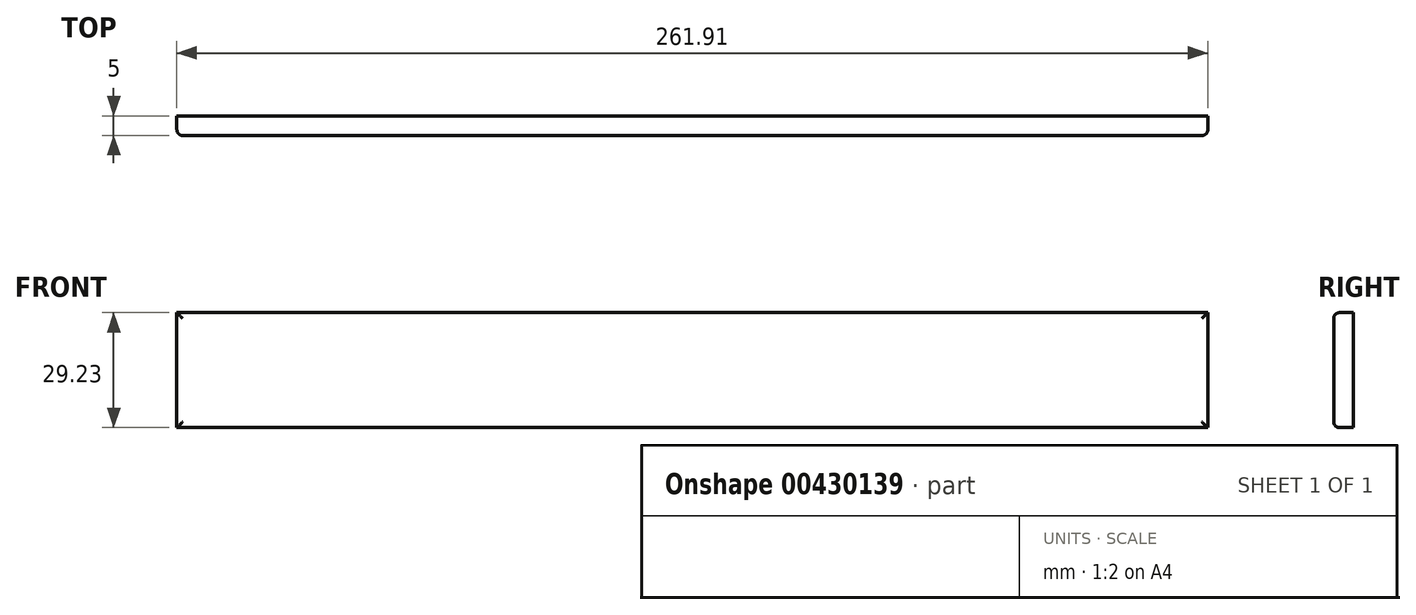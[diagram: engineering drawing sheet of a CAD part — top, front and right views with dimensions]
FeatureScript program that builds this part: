
annotation { "Feature Type Name" : "Feature", "Feature Type Description" : "" }
export const myFeature = defineFeature(function(context is Context, id is Id, definition is map)
    precondition{}
    {
        {
            var Q0;
            Q0=qCreatedBy(makeId("Front.planeOp"),FACE);
            var sketch = newSketch(context, id + "F0", { "sketchPlane" : qUnion([Q0])});
            skLineSegment(sketch, "E0.bottom", {"start": v(-90.82, 32.53) * mm, "end": v(90.82, 32.53) * mm});
            skLineSegment(sketch, "E0.top", {"start": v(-90.82, -25.4) * mm, "end": v(90.82, -25.4) * mm});
            skLineSegment(sketch, "E0.left", {"start": v(-90.82, 32.53) * mm, "end": v(-90.82, -25.4) * mm});
            skLineSegment(sketch, "E0.right", {"start": v(90.82, 32.53) * mm, "end": v(90.82, -25.4) * mm});
            skSolve(sketch);
        }
        {
            var Q0;
            Q0=makeQuery(id+"F0.imprint","IMPRINT",FACE,{"disambiguationData":[TD([[makeQuery(id+"F0.imprint","IMPRINT",EDGE,{"derivedFrom":sQuery(id+"F0.wireOp",EDGE,"E0.bottom")}),-1.0]])]});
            extrude(context, id + "F1", {"entities" : qUnion([Q0]), "depth" : 5 * mm});
        }
        {
            var Q0;
            Q0=makeQuery(id+"F1.opExtrude","SWEPT_FACE",FACE,{"disambiguationData":[OSD([sQuery(id+"F0.wireOp",EDGE,"E0.bottom")])]});
            extrude(context, id + "F2", {"entities" : qUnion([Q0]), "operationType" : NewBodyOperationType.INTERSECT, "oppositeDirection" : true, "depth" : 29.23 * mm});
        }
        {
            var Q0;
            Q0=makeQuery(id+"F1.opExtrude","SWEPT_FACE",FACE,{"disambiguationData":[OSD([sQuery(id+"F0.wireOp",EDGE,"E0.left")])]});
            extrude(context, id + "F3", {"entities" : qUnion([Q0]), "operationType" : NewBodyOperationType.ADD, "oppositeDirection" : true, "depth" : 261.91 * mm});
        }
        {
            var Q0;
            {var subQ0=sQuery(id+"F0.wireOp",EDGE,"E0.left");Q0=makeQuery(id+"F3.boolean.opBoolean","MERGE",FACE,{"derivedFrom":[makeQuery(id+"F1.opExtrude","CAP_FACE",FACE,{"disambiguationData":[OSD([sQuery(id+"F0.wireOp",EDGE,"E0.bottom"),sQuery(id+"F0.wireOp",EDGE,"E0.top"),subQ0,sQuery(id+"F0.wireOp",EDGE,"E0.right")])],"isStart":false}),makeQuery(id+"F3.opExtrude","SWEPT_FACE",FACE,{"disambiguationData":[OSD([subQ0]),TDD([makeQuery(id+"F1.opExtrude","CAP_EDGE",EDGE,{"disambiguationData":[OSD([subQ0])],"isStart":false})])]})]});}
            fillet(context, id + "F4", {"entities" : qUnion([Q0]), "radius" : 1.5 * mm, "tangentPropagation" : true, "allowEdgeOverflow" : false});
        }
    });
